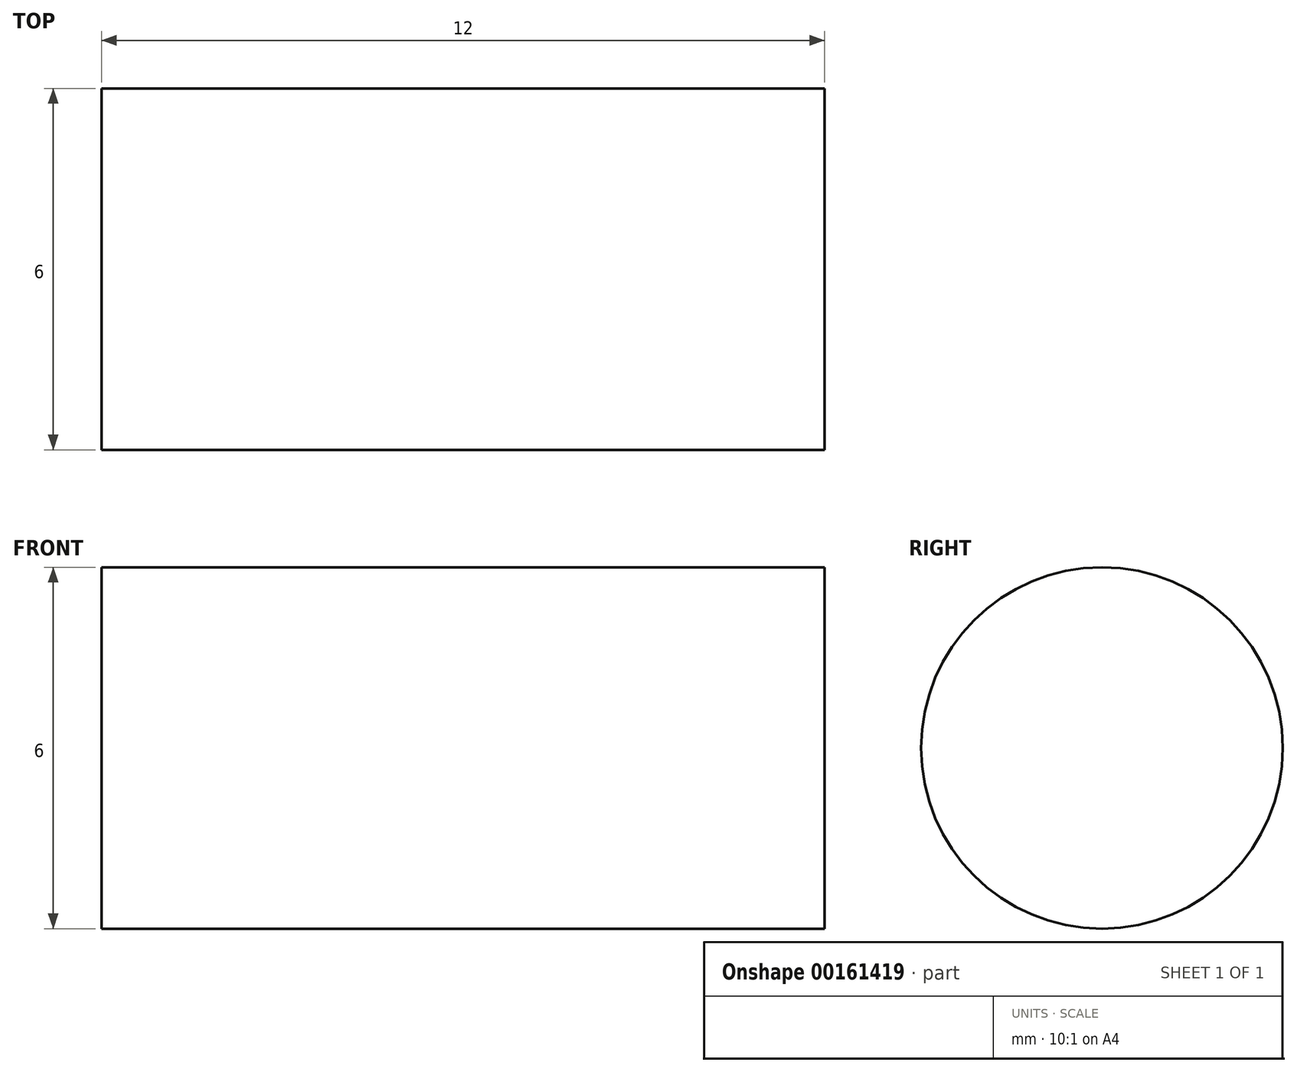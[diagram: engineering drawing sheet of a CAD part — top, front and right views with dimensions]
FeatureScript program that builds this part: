
annotation { "Feature Type Name" : "Feature", "Feature Type Description" : "" }
export const myFeature = defineFeature(function(context is Context, id is Id, definition is map)
    precondition{}
    {
        {
            var Q0;
            Q0=qCreatedBy(makeId("Right.planeOp"),FACE);
            var sketch = newSketch(context, id + "F0", { "sketchPlane" : qUnion([Q0])});
            skCircle(sketch, "E0", {"center": v(0, 0) * mm, "radius": 3 * mm});
            skSolve(sketch);
        }
        {
            var Q0;
            Q0=qSketchRegion(id+"F0",true);
            extrude(context, id + "F1", {"entities" : qUnion([Q0]), "depth" : 12 * mm});
        }
    });
